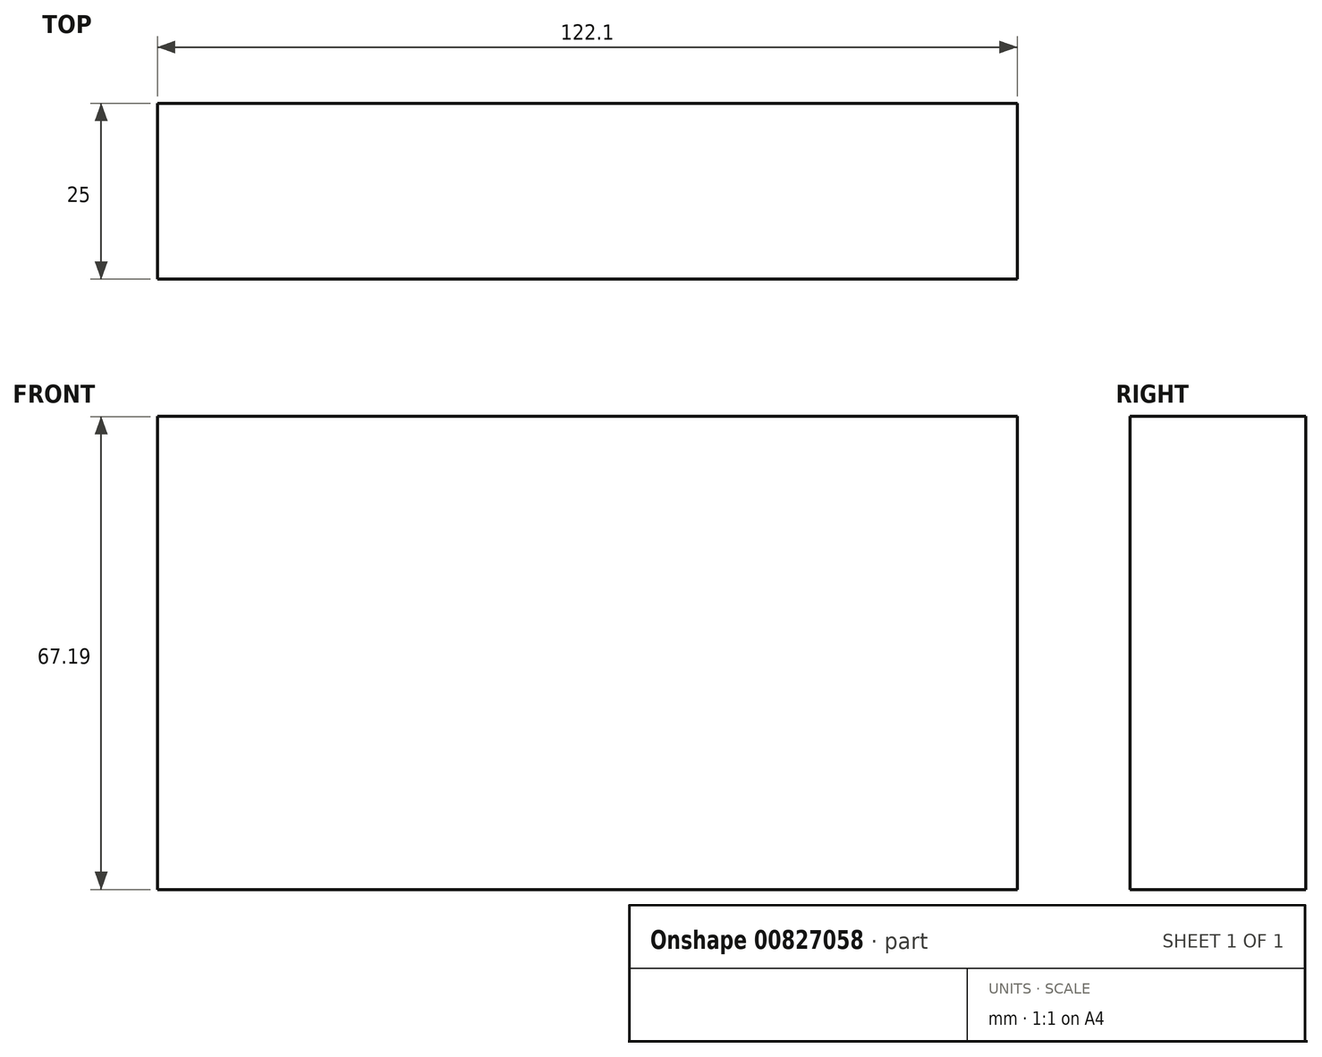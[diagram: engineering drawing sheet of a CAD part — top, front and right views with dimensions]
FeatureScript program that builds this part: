
annotation { "Feature Type Name" : "Feature", "Feature Type Description" : "" }
export const myFeature = defineFeature(function(context is Context, id is Id, definition is map)
    precondition{}
    {
        {
            var Q0;
            Q0=qCreatedBy(makeId("Front.planeOp"),FACE);
            var sketch = newSketch(context, id + "F0", { "sketchPlane" : qUnion([Q0])});
            skLineSegment(sketch, "E0.bottom", {"start": v(-59.06, 32.7) * mm, "end": v(63.04, 32.7) * mm});
            skLineSegment(sketch, "E0.top", {"start": v(-59.06, -34.5) * mm, "end": v(63.04, -34.5) * mm});
            skLineSegment(sketch, "E0.left", {"start": v(-59.06, 32.7) * mm, "end": v(-59.06, -34.5) * mm});
            skLineSegment(sketch, "E0.right", {"start": v(63.04, 32.7) * mm, "end": v(63.04, -34.5) * mm});
            skSolve(sketch);
        }
        {
            var Q0;
            Q0 = qSketchRegion(id + "F0", true);
            extrude(context, id + "F1", {"entities" : qUnion([Q0]), "depth" : 25 * mm, "offsetDistance" : 25 * mm});
        }
    });
